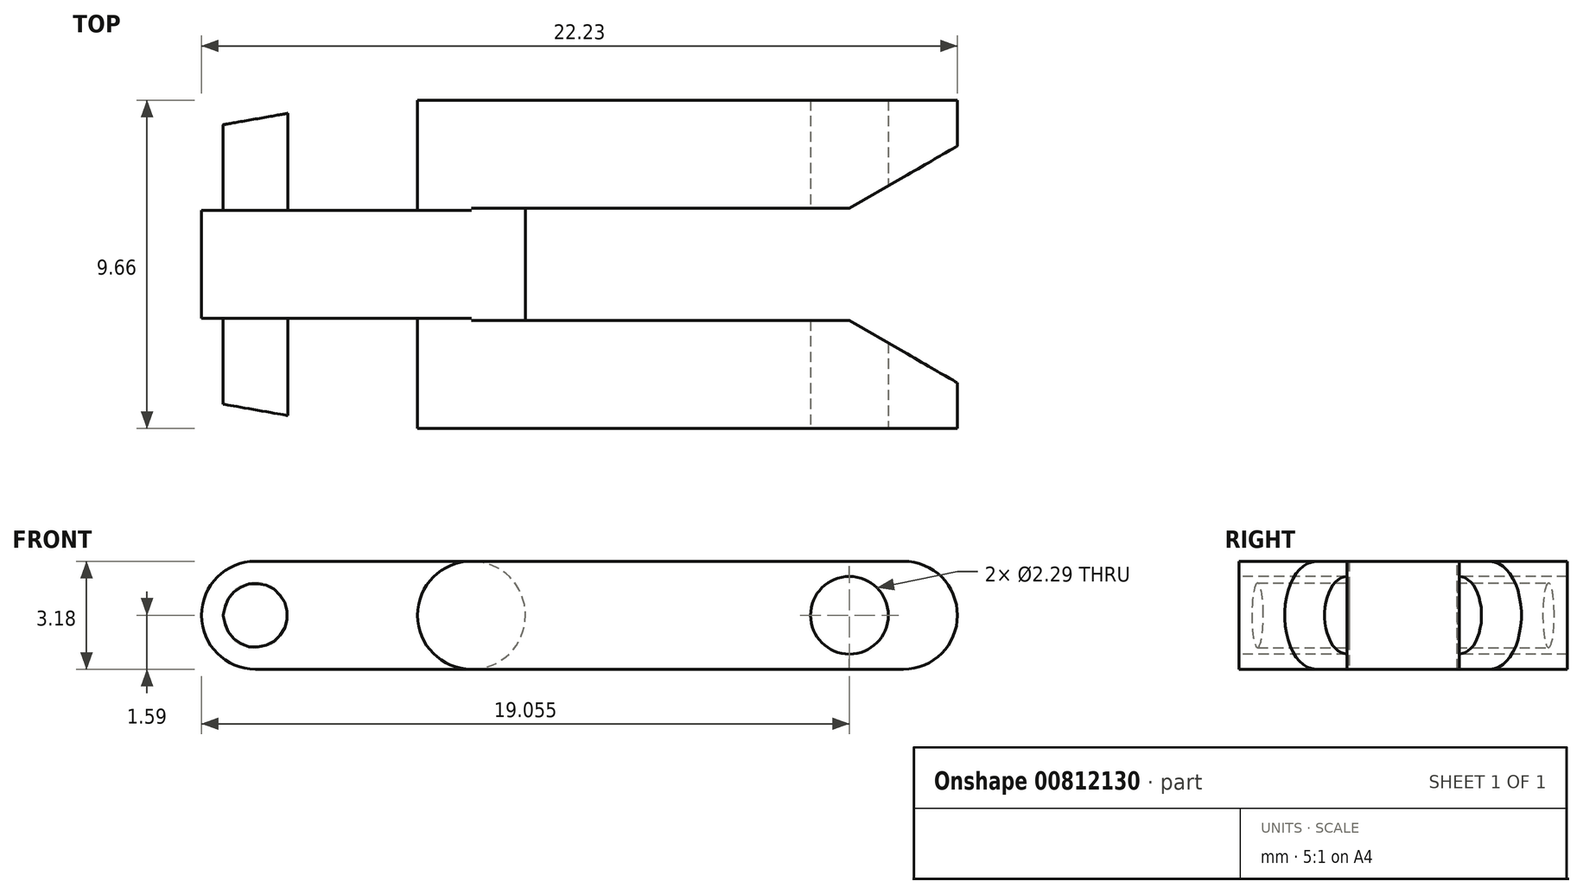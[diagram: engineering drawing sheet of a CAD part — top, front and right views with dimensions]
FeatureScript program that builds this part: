
annotation { "Feature Type Name" : "Feature", "Feature Type Description" : "" }
export const myFeature = defineFeature(function(context is Context, id is Id, definition is map)
    precondition{}
    {
        {
            var Q0;
            Q0=qCreatedBy(makeId("Top.planeOp"),FACE);
            var sketch = newSketch(context, id + "F0", { "sketchPlane" : qUnion([Q0])});
            skLineSegment(sketch, "E0", {"start": v(12.7, 4.83) * mm, "end": v(-3.18, 4.83) * mm});
            skLineSegment(sketch, "E1", {"start": v(-3.18, 4.83) * mm, "end": v(-3.18, 1.59) * mm});
            skLineSegment(sketch, "E2", {"start": v(-3.18, 1.59) * mm, "end": v(-9.53, 1.59) * mm});
            skLineSegment(sketch, "E3", {"start": v(-9.53, 1.59) * mm, "end": v(-9.53, -1.59) * mm});
            skLineSegment(sketch, "E4", {"start": v(-9.53, -1.59) * mm, "end": v(-3.18, -1.59) * mm});
            skLineSegment(sketch, "E5", {"start": v(-3.18, -1.59) * mm, "end": v(-3.18, -4.83) * mm});
            skLineSegment(sketch, "E6", {"start": v(-3.18, -4.83) * mm, "end": v(12.7, -4.83) * mm});
            skLineSegment(sketch, "E7", {"start": v(12.7, -4.83) * mm, "end": v(12.7, -1.65) * mm});
            skLineSegment(sketch, "E8", {"start": v(12.7, -1.65) * mm, "end": v(0, -1.65) * mm});
            skLineSegment(sketch, "E9", {"start": v(0, -1.65) * mm, "end": v(0, 1.65) * mm});
            skLineSegment(sketch, "E10", {"start": v(0, 1.65) * mm, "end": v(12.7, 1.65) * mm});
            skLineSegment(sketch, "E11", {"start": v(12.7, 1.65) * mm, "end": v(12.7, 4.83) * mm});
            skLineSegment(sketch, "E12", {"start": v(-3.18, 1.59) * mm, "end": v(-3.18, -1.59) * mm, "construction": true});
            skLineSegment(sketch, "E13", {"start": v(0, 0) * mm, "end": v(-3.18, 0) * mm});
            skSolve(sketch);
        }
        {
            var Q0;
            Q0 = qSketchRegion(id + "F0", true);
            extrude(context, id + "F1", {"entities" : qUnion([Q0]), "endBound" : BoundingType.SYMMETRIC, "oppositeDirection" : true, "depth" : 3.17 * mm, "offsetDistance" : 25.4 * mm});
        }
        {
            var Q0;
            Q0=qCreatedBy(makeId("Front.planeOp"),FACE);
            var sketch = newSketch(context, id + "F2", { "sketchPlane" : qUnion([Q0])});
            skCircle(sketch, "E14", {"center": v(-7.94, 0) * mm, "radius": 0.95 * mm});
            skLineSegment(sketch, "E15", {"start": v(-7.94, 0) * mm, "end": v(-9.53, 0) * mm});
            skSolve(sketch);
        }
        {
            var Q0;
            Q0 = qSketchRegion(id + "F2", true);
            extrude(context, id + "F3", {"entities" : qUnion([Q0]), "operationType" : NewBodyOperationType.ADD, "endBound" : BoundingType.SYMMETRIC, "depth" : 8.9 * mm, "offsetDistance" : 25.4 * mm});
        }
        {
            var Q0;
            Q0=makeQuery(id+"F1.opExtrude","CAP_EDGE",EDGE,{"disambiguationData":[OSD([sQuery(id+"F0.wireOp",EDGE,"E1")])],"isStart":false});
            var Q1;
            Q1=makeQuery(id+"F1.opExtrude","CAP_EDGE",EDGE,{"disambiguationData":[OSD([sQuery(id+"F0.wireOp",EDGE,"E1")])],"isStart":true});
            var Q2;
            Q2=makeQuery(id+"F1.opExtrude","CAP_EDGE",EDGE,{"disambiguationData":[OSD([sQuery(id+"F0.wireOp",EDGE,"E5")])],"isStart":true});
            var Q3;
            Q3=makeQuery(id+"F1.opExtrude","CAP_EDGE",EDGE,{"disambiguationData":[OSD([sQuery(id+"F0.wireOp",EDGE,"E5")])],"isStart":false});
            var Q4;
            Q4=makeQuery(id+"F1.opExtrude","CAP_EDGE",EDGE,{"disambiguationData":[OSD([sQuery(id+"F0.wireOp",EDGE,"E3")])],"isStart":true});
            var Q5;
            Q5=makeQuery(id+"F1.opExtrude","CAP_EDGE",EDGE,{"disambiguationData":[OSD([sQuery(id+"F0.wireOp",EDGE,"E3")])],"isStart":false});
            var Q6;
            Q6=makeQuery(id+"F1.opExtrude","CAP_EDGE",EDGE,{"disambiguationData":[OSD([sQuery(id+"F0.wireOp",EDGE,"E11")])],"isStart":false});
            var Q7;
            Q7=makeQuery(id+"F1.opExtrude","CAP_EDGE",EDGE,{"disambiguationData":[OSD([sQuery(id+"F0.wireOp",EDGE,"E11")])],"isStart":true});
            var Q8;
            Q8=makeQuery(id+"F1.opExtrude","CAP_EDGE",EDGE,{"disambiguationData":[OSD([sQuery(id+"F0.wireOp",EDGE,"E7")])],"isStart":true});
            var Q9;
            Q9=makeQuery(id+"F1.opExtrude","CAP_EDGE",EDGE,{"disambiguationData":[OSD([sQuery(id+"F0.wireOp",EDGE,"E7")])],"isStart":false});
            var Q10;
            Q10=makeQuery(id+"F1.opExtrude","CAP_EDGE",EDGE,{"disambiguationData":[OSD([sQuery(id+"F0.wireOp",EDGE,"E9")])],"isStart":true});
            var Q11;
            Q11=makeQuery(id+"F1.opExtrude","CAP_EDGE",EDGE,{"disambiguationData":[OSD([sQuery(id+"F0.wireOp",EDGE,"E9")])],"isStart":false});
            fillet(context, id + "F4", {"entities" : qUnion([Q0, Q1, Q2, Q3, Q4, Q5, Q6, Q7, Q8, Q9, Q10, Q11]), "radius" : 1.59 * mm, "tangentPropagation" : true, "allowEdgeOverflow" : false});
        }
        {
            var Q0;
            Q0=qCreatedBy(makeId("Front.planeOp"),FACE);
            var sketch = newSketch(context, id + "F5", { "sketchPlane" : qUnion([Q0])});
            skLineSegment(sketch, "E16", {"start": v(11.11, 1.59) * mm, "end": v(11.11, -1.59) * mm});
            skCircle(sketch, "E17", {"center": v(9.53, 0) * mm, "radius": 1.14 * mm});
            skLineSegment(sketch, "E18", {"start": v(9.53, 0) * mm, "end": v(11.11, 0) * mm});
            skSolve(sketch);
        }
        {
            var Q0;
            Q0 = qSketchRegion(id + "F5", true);
            extrude(context, id + "F6", {"entities" : qUnion([Q0]), "operationType" : NewBodyOperationType.REMOVE, "endBound" : BoundingType.SYMMETRIC, "oppositeDirection" : true, "depth" : 25.4 * mm, "offsetDistance" : 25.4 * mm});
        }
        {
            var Q0;
            Q0=qCreatedBy(makeId("Top.planeOp"),FACE);
            var sketch = newSketch(context, id + "F7", { "sketchPlane" : qUnion([Q0])});
            skLineSegment(sketch, "E19", {"start": v(9.53, -1.65) * mm, "end": v(15.88, -5.32) * mm});
            skLineSegment(sketch, "E20", {"start": v(15.88, -5.32) * mm, "end": v(15.88, 5.32) * mm});
            skLineSegment(sketch, "E21", {"start": v(-9.53, 4) * mm, "end": v(-6.99, 4.45) * mm});
            skLineSegment(sketch, "E22", {"start": v(-6.99, 4.45) * mm, "end": v(-9.53, 4.44) * mm});
            skLineSegment(sketch, "E23", {"start": v(-9.53, 4.44) * mm, "end": v(-9.53, 4) * mm});
            skLineSegment(sketch, "E24", {"start": v(-6.99, -4.45) * mm, "end": v(-9.53, -4) * mm});
            skLineSegment(sketch, "E25", {"start": v(-9.53, -4) * mm, "end": v(-9.53, -4.45) * mm});
            skLineSegment(sketch, "E26", {"start": v(-9.53, -4.45) * mm, "end": v(-6.99, -4.45) * mm});
            skLineSegment(sketch, "E27", {"start": v(15.88, 5.32) * mm, "end": v(9.52, 1.65) * mm});
            skLineSegment(sketch, "E28", {"start": v(9.53, 1.65) * mm, "end": v(9.53, -1.65) * mm});
            skSolve(sketch);
        }
        {
            var Q0;
            Q0 = qSketchRegion(id + "F7", true);
            extrude(context, id + "F8", {"entities" : qUnion([Q0]), "operationType" : NewBodyOperationType.REMOVE, "endBound" : BoundingType.SYMMETRIC, "oppositeDirection" : true, "depth" : 25.4 * mm, "offsetDistance" : 25.4 * mm});
        }
    });
